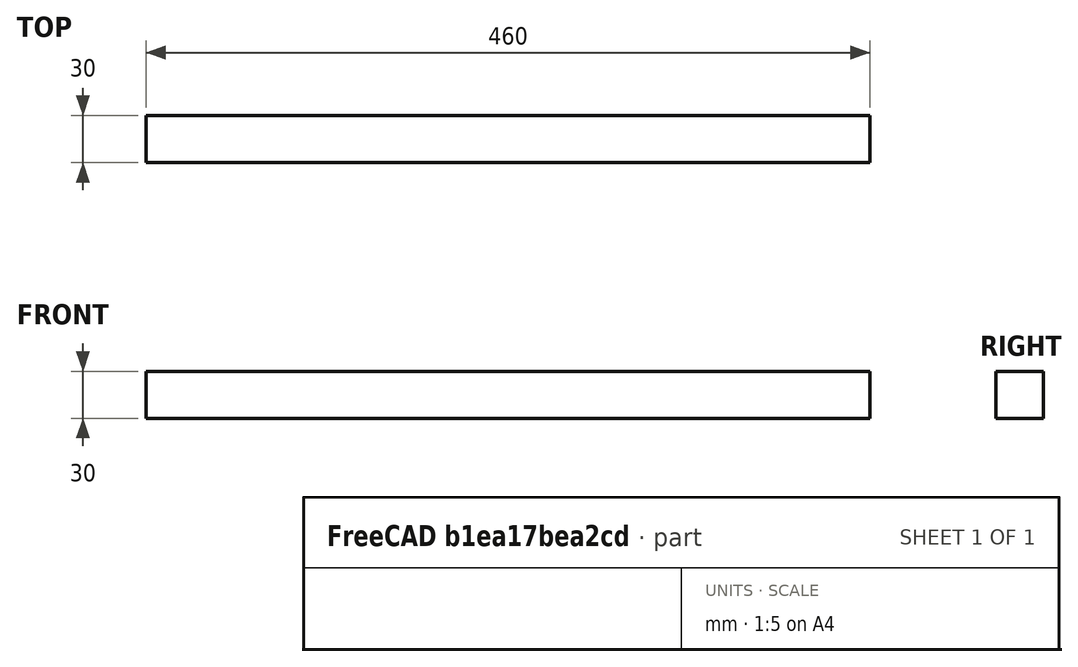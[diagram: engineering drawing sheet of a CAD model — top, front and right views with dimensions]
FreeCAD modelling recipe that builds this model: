
FCSTD DOCUMENT  (FreeCAD 0.20R29177 (Git))
Label: framesideleft
License: All rights reserved
LicenseURL: http://en.wikipedia.org/wiki/All_rights_reserved
objects: Sketcher::SketchObject×1, PartDesign::Pad×1, PartDesign::Body×1
note: 4 computed .brp shape members not serialized (recipe doc carries the construction recipe); baked Part::Feature solids carry a one-line shape summary decoded from their .brp

FEATURE [Sketcher::SketchObject] Sketch
  FullyConstrained = true
  MapMode = 5
  Placement = pos=(0,0,0) rot=(0.57735,0.57735,0.57735;2.0944rad)
  Support = -> [YZ_Plane]
  sketch-geometry (4):
    g0: LineSegment StartX=0 StartY=0 StartZ=0 EndX=30 EndY=0 EndZ=0
    g1: LineSegment StartX=30 StartY=0 StartZ=0 EndX=30 EndY=30 EndZ=0
    g2: LineSegment StartX=30 StartY=30 StartZ=0 EndX=0 EndY=30 EndZ=0
    g3: LineSegment StartX=0 StartY=30 StartZ=0 EndX=0 EndY=0 EndZ=0
  constraints (11):
    c: Coincident(g0,g1)
    c: Coincident(g1,g2)
    c: Coincident(g2,g3)
    c: Coincident(g3,g0)
    c: Horizontal(g0)
    c: Horizontal(g2)
    c: Vertical(g1)
    c: Vertical(g3)
    c: Coincident(g0,g-1)
    c: Equal(g1,g2)
    c: DistanceX(g0,g0) = 30
FEATURE [PartDesign::Pad] Pad
  Direction = (1,1,1)
  Length = 460
  Length2 = 100
  Placement = pos=(0,0,0) rot=(0.57735,0.57735,0.57735;2.0944rad)
  Profile = -> Sketch
  Type = 0
FEATURE [PartDesign::Body] Body  label="framesideleft"
  Group = -> [Sketch,Pad]
  Origin = -> Origin
  Tip = -> Pad
